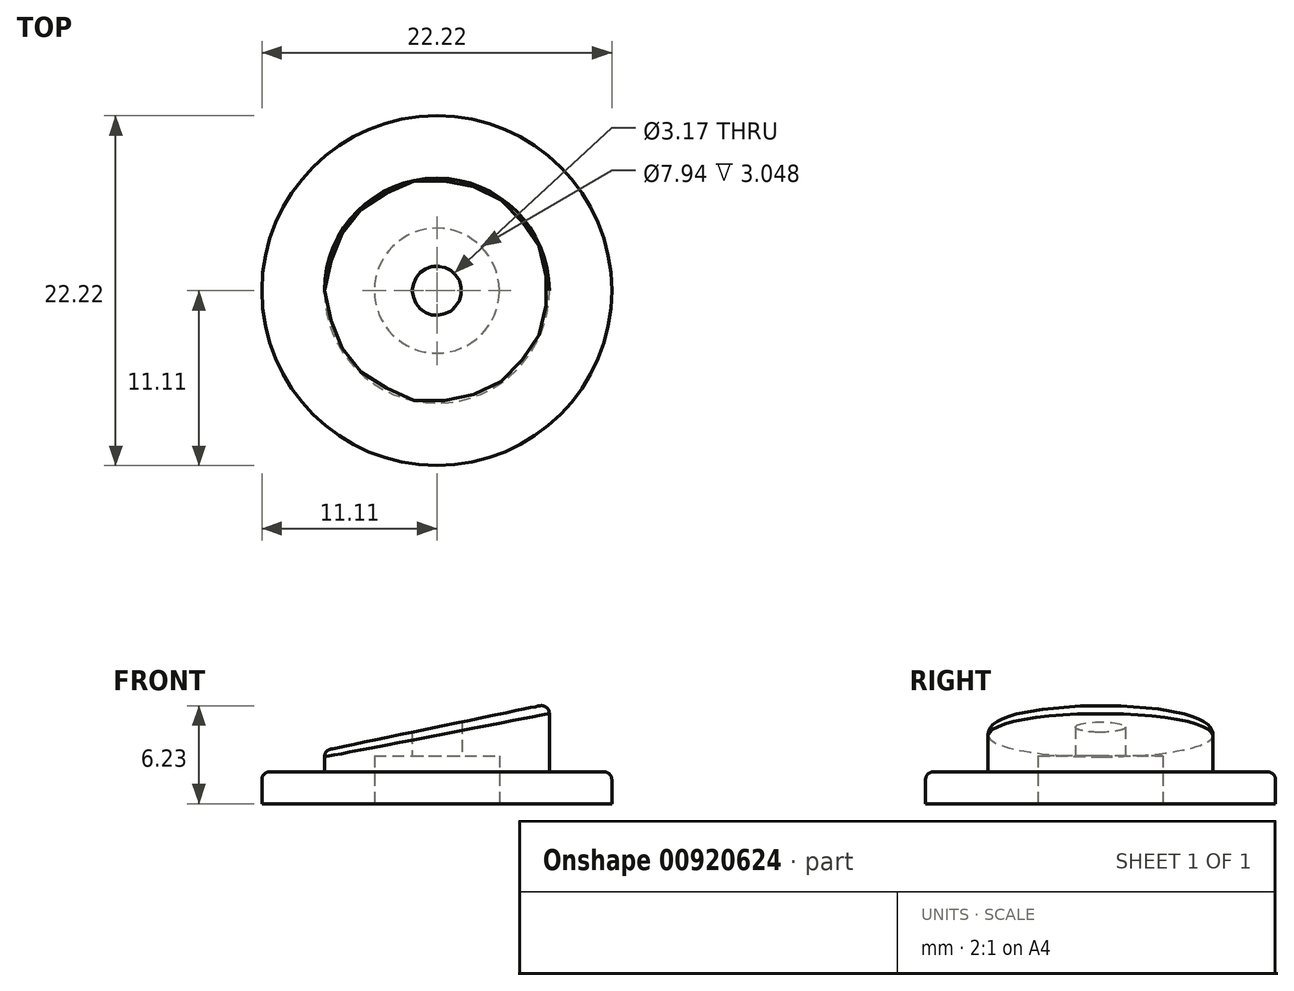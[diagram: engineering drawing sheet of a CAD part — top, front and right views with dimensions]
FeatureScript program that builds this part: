
annotation { "Feature Type Name" : "Feature", "Feature Type Description" : "" }
export const myFeature = defineFeature(function(context is Context, id is Id, definition is map)
    precondition{}
    {
        {
            var Q0;
            Q0=qCreatedBy(makeId("Top.planeOp"),FACE);
            var sketch = newSketch(context, id + "F0", { "sketchPlane" : qUnion([Q0])});
            skCircle(sketch, "E0", {"center": v(0, 0) * mm, "radius": 11.11 * mm});
            skCircle(sketch, "E1", {"center": v(0, 0) * mm, "radius": 7.14 * mm});
            skCircle(sketch, "E2", {"center": v(0, 0) * mm, "radius": 1.59 * mm});
            skSolve(sketch);
        }
        {
            var Q0;
            Q0=makeQuery(id+"F0.imprint","IMPRINT",FACE,{"disambiguationData":[TD([[makeQuery(id+"F0.imprint","IMPRINT",EDGE,{"derivedFrom":sQuery(id+"F0.wireOp",EDGE,"E0")}),1.0]])]});
            extrude(context, id + "F1", {"entities" : qUnion([Q0]), "depth" : 2.03 * mm, "offsetDistance" : 25.4 * mm});
        }
        {
            var Q0;
            Q0=makeQuery(id+"F0.imprint","IMPRINT",FACE,{"disambiguationData":[TD([[makeQuery(id+"F0.imprint","IMPRINT",EDGE,{"derivedFrom":sQuery(id+"F0.wireOp",EDGE,"E1")}),1.0]])]});
            extrude(context, id + "F2", {"entities" : qUnion([Q0]), "operationType" : NewBodyOperationType.ADD, "depth" : 6.35 * mm, "offsetDistance" : 25.4 * mm});
        }
        {
            var Q0;
            Q0=qCreatedBy(makeId("Front.planeOp"),FACE);
            var sketch = newSketch(context, id + "F3", { "sketchPlane" : qUnion([Q0])});
            skLineSegment(sketch, "E3.0", {"start": v(-7.14, 6.35) * mm, "end": v(7.14, 6.35) * mm});
            skLineSegment(sketch, "E4", {"start": v(-7.14, 2.03) * mm, "end": v(-7.14, 6.35) * mm});
            skLineSegment(sketch, "E5", {"start": v(7.14, 6.35) * mm, "end": v(7.14, 2.03) * mm});
            skLineSegment(sketch, "E6", {"start": v(7.14, 6.35) * mm, "end": v(-7.14, 3.39) * mm});
            skSolve(sketch);
        }
        {
            var Q0;
            {var subQ0=sQuery(id+"F3.wireOp",EDGE,"E3.0");Q0=makeQuery(id+"F3.imprint","IMPRINT",FACE,{"disambiguationData":[TD([[makeQuery(id+"F3.imprint","IMPRINT",EDGE,{"derivedFrom":subQ0}),-1.0]])]});}
            extrude(context, id + "F4", {"entities" : qUnion([Q0]), "operationType" : NewBodyOperationType.REMOVE, "endBound" : BoundingType.THROUGH_ALL, "oppositeDirection" : true, "depth" : 25.4 * mm, "offsetDistance" : 25.4 * mm, "hasSecondDirection" : true, "secondDirectionBound" : SecondDirectionBoundingType.THROUGH_ALL, "secondDirectionOppositeDirection" : false, "secondDirectionDepth" : 25.4 * mm});
        }
        {
            var Q0;
            {var subQ0=sQuery(id+"F0.wireOp",EDGE,"E1");Q0=makeQuery(id+"F2.boolean.opBoolean","MERGE",FACE,{"derivedFrom":[makeQuery(id+"F1.opExtrude","CAP_FACE",FACE,{"disambiguationData":[OSD([sQuery(id+"F0.wireOp",EDGE,"E0"),subQ0])],"isStart":true}),makeQuery(id+"F2.opExtrude","CAP_FACE",FACE,{"disambiguationData":[OSD([subQ0,sQuery(id+"F0.wireOp",EDGE,"E2")])],"isStart":true})]});}
            var sketch = newSketch(context, id + "F5", { "sketchPlane" : qUnion([Q0])});
            skCircle(sketch, "E7", {"center": v(0, 0) * mm, "radius": 3.97 * mm});
            skSolve(sketch);
        }
        {
            var Q0;
            Q0=makeQuery(id+"F5.imprint","IMPRINT",FACE,{"disambiguationData":[TD([[makeQuery(id+"F5.imprint","IMPRINT",EDGE,{"derivedFrom":sQuery(id+"F5.wireOp",EDGE,"E7")}),1.0]])]});
            extrude(context, id + "F6", {"entities" : qUnion([Q0]), "operationType" : NewBodyOperationType.REMOVE, "oppositeDirection" : true, "depth" : 3.05 * mm, "offsetDistance" : 25.4 * mm});
        }
        {
            var Q0;
            Q0=makeQuery(id+"F4.boolean.opBoolean","INTERSECT",EDGE,{"derivedFrom":[makeQuery(id+"F2.opExtrude","SWEPT_FACE",FACE,{"disambiguationData":[OSD([sQuery(id+"F0.wireOp",EDGE,"E1")])]}),makeQuery(id+"F4.opExtrude","SWEPT_FACE",FACE,{"disambiguationData":[OSD([sQuery(id+"F3.wireOp",EDGE,"E6")])]})]});
            var Q1;
            Q1=makeQuery(id+"F1.opExtrude","CAP_EDGE",EDGE,{"disambiguationData":[OSD([sQuery(id+"F0.wireOp",EDGE,"E0")])],"isStart":false});
            fillet(context, id + "F7", {"entities" : qUnion([Q0, Q1]), "radius" : 0.5 * mm, "tangentPropagation" : true, "allowEdgeOverflow" : false});
        }
    });
